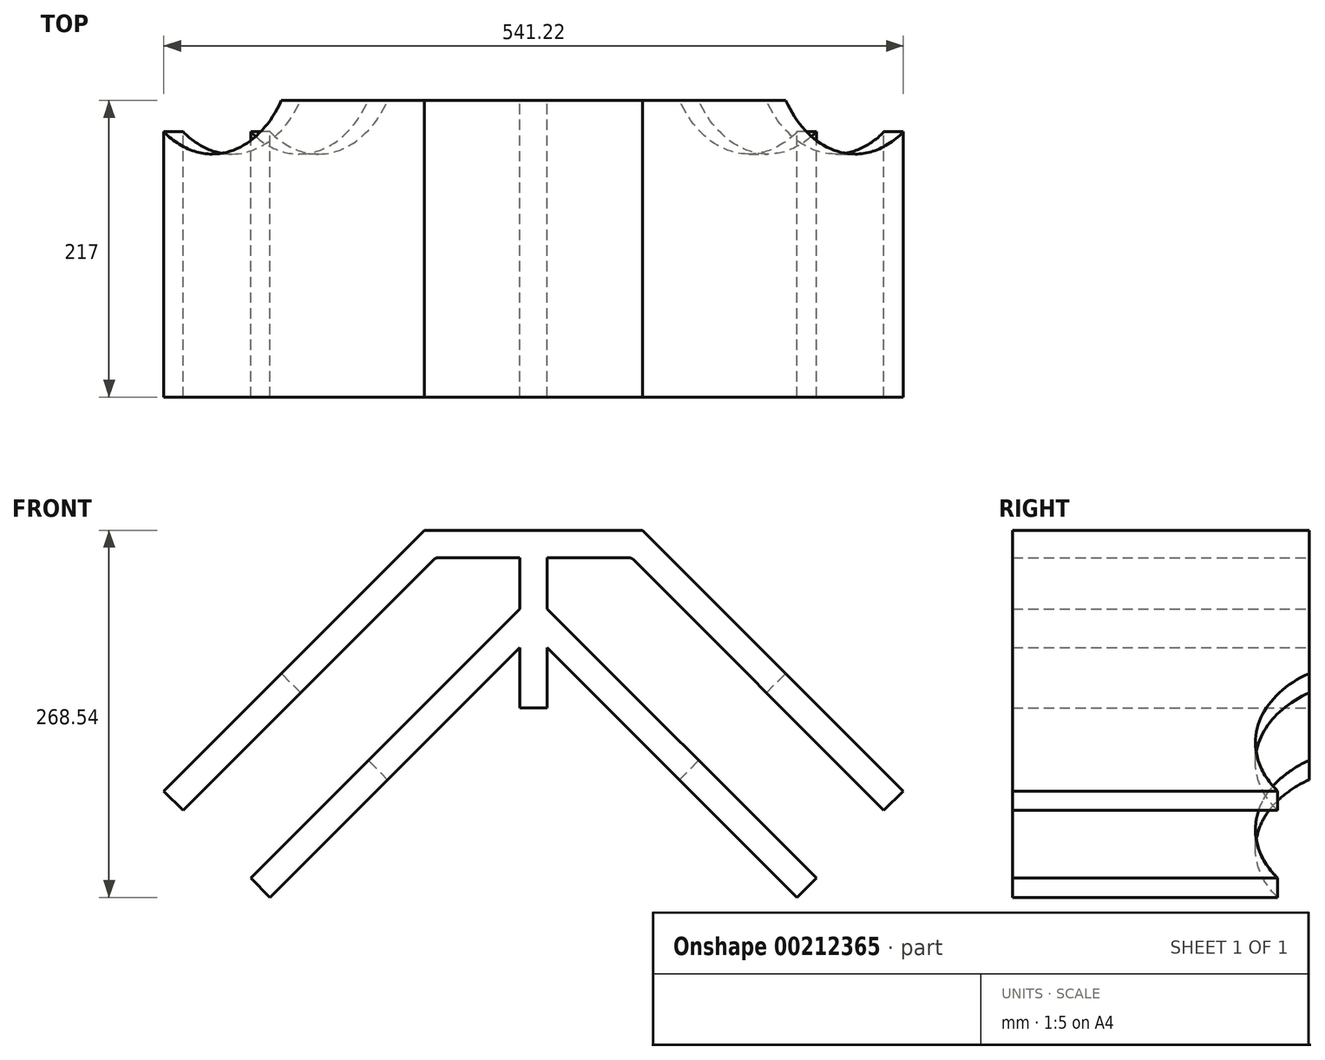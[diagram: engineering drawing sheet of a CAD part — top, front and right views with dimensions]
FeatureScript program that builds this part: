
annotation { "Feature Type Name" : "Feature", "Feature Type Description" : "" }
export const myFeature = defineFeature(function(context is Context, id is Id, definition is map)
    precondition{}
    {
        {
            var Q0;
            Q0=qCreatedBy(makeId("Front.planeOp"),FACE);
            var sketch = newSketch(context, id + "F0", { "sketchPlane" : qUnion([Q0])});
            skLineSegment(sketch, "E0", {"start": v(-270.61, 46.36) * mm, "end": v(-79.86, 237.11) * mm});
            skLineSegment(sketch, "E1", {"start": v(270.61, 46.36) * mm, "end": v(79.86, 237.11) * mm});
            skLineSegment(sketch, "E2.0", {"start": v(-256.47, 32.21) * mm, "end": v(-73.04, 215.65) * mm});
            skLineSegment(sketch, "E3", {"start": v(-79.86, 237.11) * mm, "end": v(79.86, 237.11) * mm});
            skLineSegment(sketch, "E4.0", {"start": v(-69.5, 217.11) * mm, "end": v(-10, 217.11) * mm});
            skLineSegment(sketch, "E5.0", {"start": v(256.47, 32.21) * mm, "end": v(73.04, 215.65) * mm});
            skArc(sketch, "E6.filletArc", {"start": v(-69.5, 217.11) * mm, "mid": v(-71.42, 216.73) * mm, "end": v(-73.04, 215.65) * mm});
            skArc(sketch, "E7.filletArc", {"start": v(73.04, 215.65) * mm, "mid": v(71.42, 216.73) * mm, "end": v(69.5, 217.11) * mm});
            skLineSegment(sketch, "E8", {"start": v(-270.61, 46.36) * mm, "end": v(-256.47, 32.21) * mm});
            skLineSegment(sketch, "E9", {"start": v(256.47, 32.21) * mm, "end": v(270.61, 46.36) * mm});
            skLineSegment(sketch, "E10.0", {"start": v(-206.97, -17.28) * mm, "end": v(-23.54, 166.15) * mm});
            skLineSegment(sketch, "E11.0", {"start": v(-192.83, -31.43) * mm, "end": v(-10, 151.4) * mm});
            skLineSegment(sketch, "E12.0", {"start": v(-10, 151.4) * mm, "end": v(-10, 107.11) * mm});
            skLineSegment(sketch, "E13.0", {"start": v(10, 217.11) * mm, "end": v(10, 179.69) * mm});
            skLineSegment(sketch, "E14.0", {"start": v(-10, 217.11) * mm, "end": v(-10, 179.69) * mm});
            skLineSegment(sketch, "E15", {"start": v(-206.97, -17.28) * mm, "end": v(-192.83, -31.43) * mm});
            skLineSegment(sketch, "E16", {"start": v(-10, 107.11) * mm, "end": v(10, 107.11) * mm});
            skLineSegment(sketch, "E17.trimOffspring", {"start": v(10, 217.11) * mm, "end": v(69.5, 217.11) * mm});
            skLineSegment(sketch, "E18", {"start": v(-23.54, 166.15) * mm, "end": v(-10, 179.69) * mm});
            skLineSegment(sketch, "E19", {"start": v(0, 107.11) * mm, "end": v(0, 81.37) * mm});
            skPoint(sketch, "E19.endSnap0", {"position": v(0, 107.11) * mm});
            skLineSegment(sketch, "E20.MirrorCS", {"start": v(23.54, 166.15) * mm, "end": v(10, 179.69) * mm});
            skLineSegment(sketch, "E21.MirrorCS", {"start": v(206.97, -17.28) * mm, "end": v(192.83, -31.43) * mm});
            skLineSegment(sketch, "E22.MirrorCS", {"start": v(192.83, -31.43) * mm, "end": v(10, 151.4) * mm});
            skLineSegment(sketch, "E23.MirrorCS", {"start": v(206.97, -17.28) * mm, "end": v(23.54, 166.15) * mm});
            skLineSegment(sketch, "E24.trimOffspring", {"start": v(10, 151.4) * mm, "end": v(10, 107.11) * mm});
            skSolve(sketch);
        }
        {
            var Q0;
            Q0=makeQuery(id+"F0.imprint","IMPRINT",FACE,{"disambiguationData":[TD([[makeQuery(id+"F0.imprint","IMPRINT",EDGE,{"derivedFrom":sQuery(id+"F0.wireOp",EDGE,"E0")}),-1.0]])]});
            extrude(context, id + "F1", {"entities" : qUnion([Q0]), "depth" : 217 * mm});
        }
        {
            var Q0;
            Q0=makeQuery(id+"F1.opExtrude","SWEPT_FACE",FACE,{"disambiguationData":[OSD([sQuery(id+"F0.wireOp",EDGE,"E0")])]});
            var sketch = newSketch(context, id + "F2", { "sketchPlane" : qUnion([Q0])});
            skCircle(sketch, "E25", {"center": v(-45.8, -108.5) * mm, "radius": 85 * mm});
            skSolve(sketch);
        }
        {
            var Q0;
            Q0=makeQuery(id+"F2.imprint","IMPRINT",FACE,{"disambiguationData":[TD([[makeQuery(id+"F2.imprint","IMPRINT",EDGE,{"derivedFrom":sQuery(id+"F2.wireOp",EDGE,"E25")}),1.0]])]});
            extrude(context, id + "F3", {"entities" : qUnion([Q0]), "operationType" : NewBodyOperationType.REMOVE, "oppositeDirection" : true, "depth" : 120 * mm});
        }
        {
            var Q0;
            Q0=makeQuery(id+"F1.opExtrude","SWEPT_FACE",FACE,{"disambiguationData":[OSD([sQuery(id+"F0.wireOp",EDGE,"E1")])]});
            var sketch = newSketch(context, id + "F4", { "sketchPlane" : qUnion([Q0])});
            skCircle(sketch, "E26", {"center": v(45.8, -108.5) * mm, "radius": 85 * mm});
            skSolve(sketch);
        }
        {
            var Q0;
            Q0=makeQuery(id+"F4.imprint","IMPRINT",FACE,{"disambiguationData":[TD([[makeQuery(id+"F4.imprint","IMPRINT",EDGE,{"derivedFrom":sQuery(id+"F4.wireOp",EDGE,"E26")}),1.0]])]});
            extrude(context, id + "F5", {"entities" : qUnion([Q0]), "operationType" : NewBodyOperationType.REMOVE, "oppositeDirection" : true, "depth" : 120 * mm});
        }
    });
